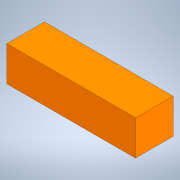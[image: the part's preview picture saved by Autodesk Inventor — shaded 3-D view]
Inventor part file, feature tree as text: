
AUTODESK INVENTOR PART (.ipt)
format: ipt  version: 2020.2 (Build 242310000, 310)  size: 96,768 bytes
history: native  units: mm
features: extrude x1, sketch x1
ambient origin geometry x8: Origin, YZ Plane, XZ Plane, XY Plane, X Axis, Y Axis, Z Axis, Center Point
bodies: Solid1 (feature_tree)
feature tree (2):
  extrude  "Extrusion1"  Depth=34.5mm
  sketch  "Sketch1"  dims[d0=118.0mm d1=34.5mm d2=32.0mm d3=0.0mm]
